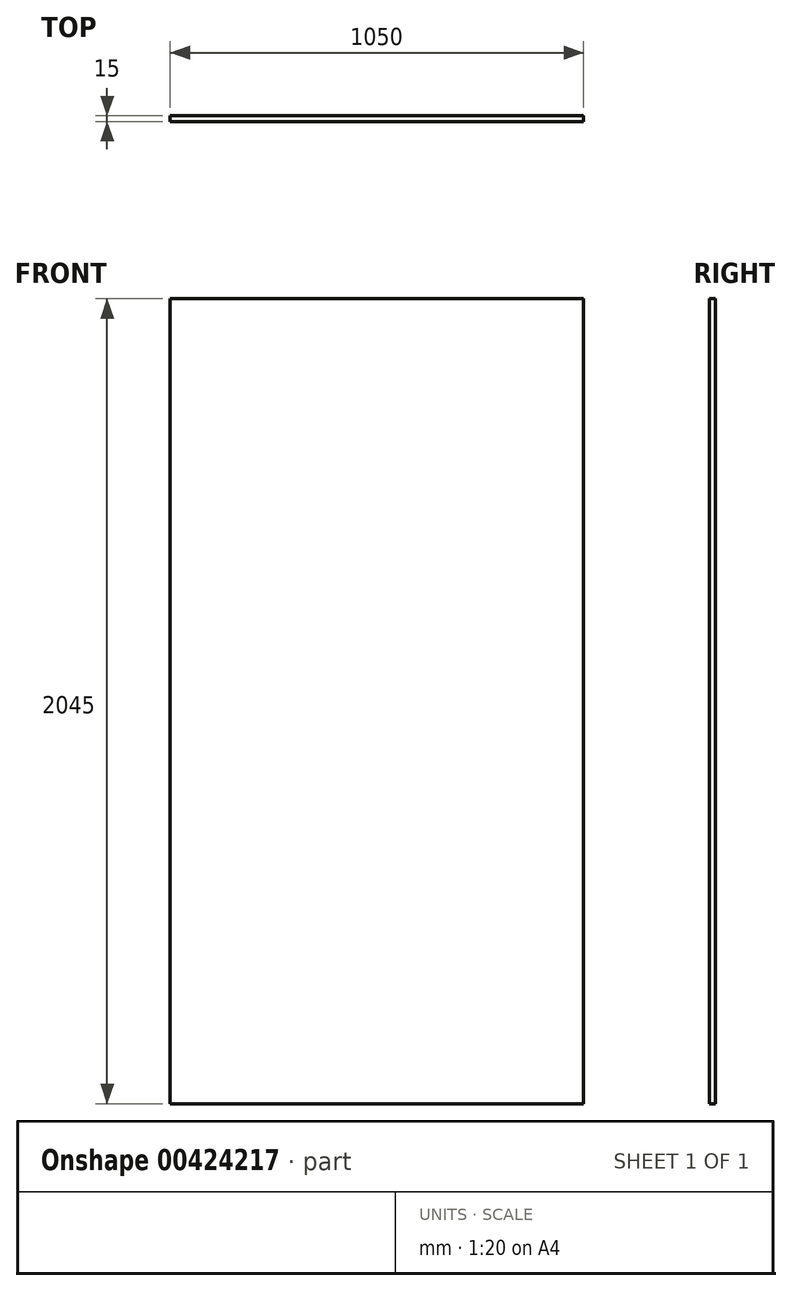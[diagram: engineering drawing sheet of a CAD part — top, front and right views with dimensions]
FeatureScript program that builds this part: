
annotation { "Feature Type Name" : "Feature", "Feature Type Description" : "" }
export const myFeature = defineFeature(function(context is Context, id is Id, definition is map)
    precondition{}
    {
        {
            var Q0;
            Q0=qCreatedBy(makeId("Front.planeOp"),FACE);
            var sketch = newSketch(context, id + "F0", { "sketchPlane" : qUnion([Q0])});
            skLineSegment(sketch, "E0.bottom", {"start": v(-524.72, 1331.03) * mm, "end": v(525.28, 1331.03) * mm});
            skLineSegment(sketch, "E0.top", {"start": v(-524.72, -713.97) * mm, "end": v(525.28, -713.97) * mm});
            skLineSegment(sketch, "E0.left", {"start": v(-524.72, 1331.03) * mm, "end": v(-524.72, -713.97) * mm});
            skLineSegment(sketch, "E0.right", {"start": v(525.28, 1331.03) * mm, "end": v(525.28, -713.97) * mm});
            skSolve(sketch);
        }
        {
            var Q0;
            Q0=makeQuery(id+"F0.imprint","IMPRINT",FACE,{"disambiguationData":[TD([[makeQuery(id+"F0.imprint","IMPRINT",EDGE,{"derivedFrom":sQuery(id+"F0.wireOp",EDGE,"E0.bottom")}),-1.0]])]});
            extrude(context, id + "F1", {"entities" : qUnion([Q0]), "depth" : 15 * mm});
        }
    });
